# Revit family: TowelRail_SurfaceMount_Nero_Celia_Hand
name_source: partatom
category: Specialty Equipment
units: mm (PartAtom-declared; Revit-internal decimal feet)

## family parameters
Always vertical = Yes
Cut with Voids When Loaded = Yes
Maintain Annotation Orientation = No
OmniClass Number = 23.31.25.25
OmniClass Title = Towel Bars
Part Type = Normal
Room Calculation Point = No
Round Connector Dimension = Use Diameter
Shared = No
Work Plane-Based = No

## types (3) — shared parameters
Assembly Code = C1030210
IfcExportAs = IfcFurniture
IfcExportType = NOTDEFINED
Manufacturer = Nero
ManufacturerOverallDepth = 70 mm
ManufacturerOverallHeight = 26 mm
ManufacturerOverallWidth = 265 mm  [stored 0.869423 ft]
ManufacturerURLProductSpecific = https://nerotapware.com.au
ModifiedIssue = 20240428 $
URL = https://nerotapware.com.au
Uniclass2015Code = Pr_40_20_76_90
Uniclass2015Title = Towel rails
Uniclass2015Version = Products v1.28
zero-valued in all types: Default Elevation

## per-type parameters (varying)
| type | BodyMaterial | Description | ManufacturerSpecCode | Model | Type Comments |
| Brushed Nickel (NR4680BN) | Metal_Nickel_Nero_Brushed | Celia Hand Towel Rail Brushed Nickel | NR4680BN | NR4680BN | Towel Rail - Surface Mount - Hand - Brushed Nickel |
| Matte Black (NR4680MB) | Metal_MatteBlack_Nero | Celia Hand Towel Rail Matte Black | NR4680MB | NR4680MB | Towel Rail - Surface Mount - Hand - Matte Black |
| Chrome (NR4680CH) | Metal_Chrome_Nero | Celia Hand Towel Rail Chrome | NR4680CH | NR4680CH | Towel Rail - Surface Mount - Hand - Chrome |

note: [stored X ft] marks values corroborated as IEEE doubles in the binary element streams (Revit-internal decimal feet)

## geometry (parser evidence)
native form markers: Sweep x3
no freeform markers — native parametric forms only
